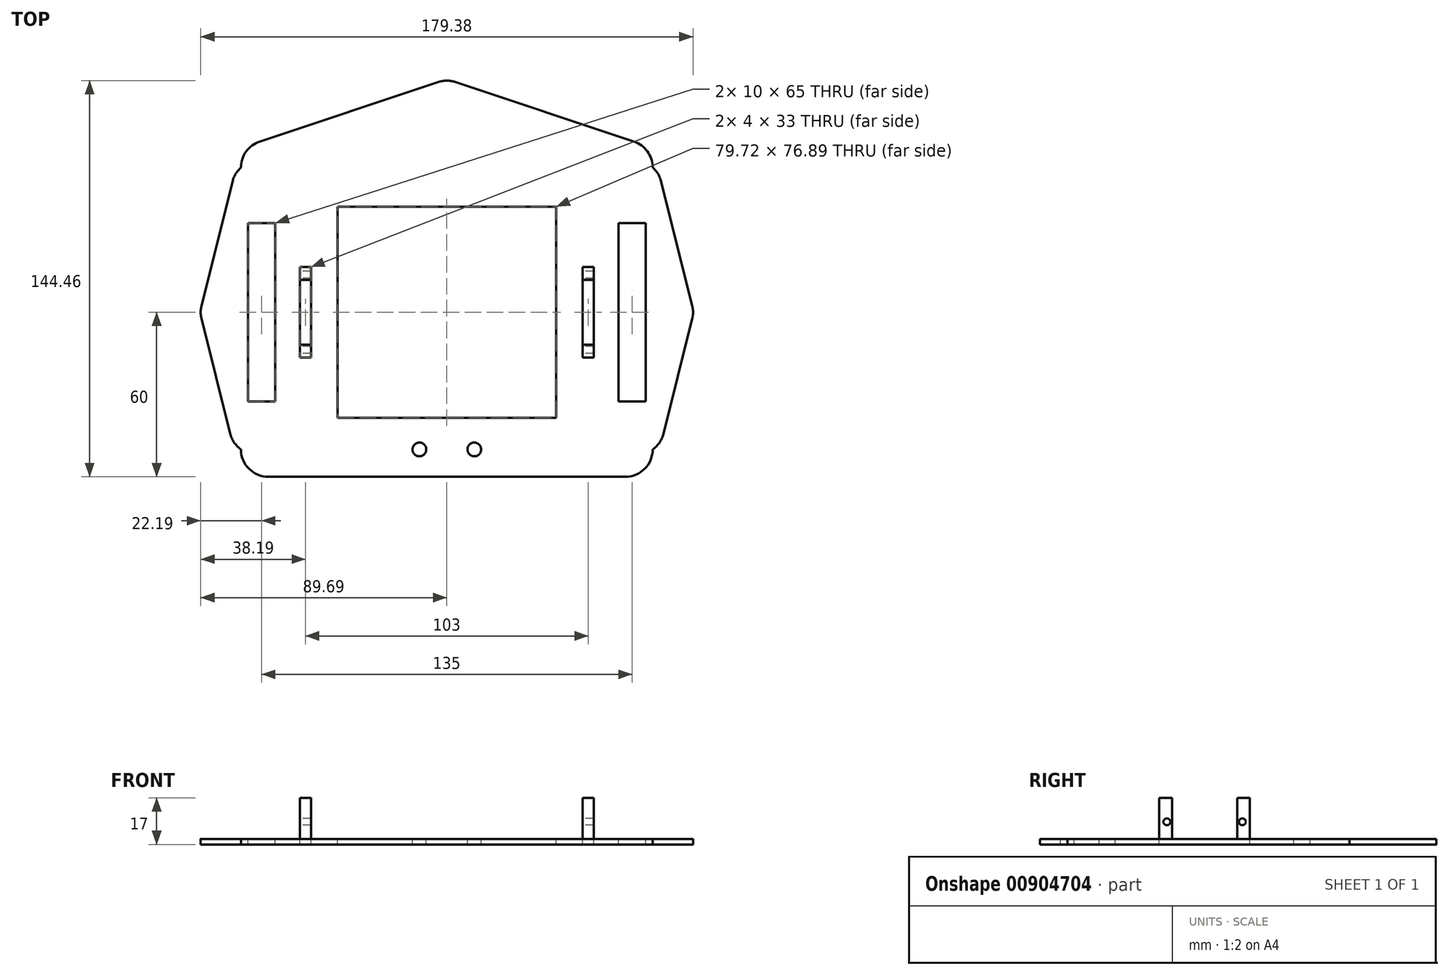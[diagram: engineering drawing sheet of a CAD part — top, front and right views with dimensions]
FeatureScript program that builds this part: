
annotation { "Feature Type Name" : "Feature", "Feature Type Description" : "" }
export const myFeature = defineFeature(function(context is Context, id is Id, definition is map)
    precondition{}
    {
        {
            var Q0;
            Q0=qCreatedBy(makeId("Top.planeOp"),FACE);
            var sketch = newSketch(context, id + "F0", { "sketchPlane" : qUnion([Q0])});
            skLineSegment(sketch, "E0.bottom", {"start": v(-75, 60) * mm, "end": v(75, 60) * mm});
            skLineSegment(sketch, "E0.top", {"start": v(-75, -60) * mm, "end": v(75, -60) * mm});
            skLineSegment(sketch, "E0.left", {"start": v(-75, 60) * mm, "end": v(-75, -60) * mm});
            skLineSegment(sketch, "E0.right", {"start": v(75, 60) * mm, "end": v(75, -60) * mm});
            skPoint(sketch, "E0.middle", {"position": v(0, 0) * mm});
            skLineSegment(sketch, "E1", {"start": v(-75, 0) * mm, "end": v(75, 0) * mm, "construction": true});
            skLineSegment(sketch, "E2.bottom", {"start": v(-62.5, 32.5) * mm, "end": v(-72.5, 32.5) * mm});
            skLineSegment(sketch, "E2.top", {"start": v(-62.5, -32.5) * mm, "end": v(-72.5, -32.5) * mm});
            skLineSegment(sketch, "E2.left", {"start": v(-62.5, 32.5) * mm, "end": v(-62.5, -32.5) * mm});
            skLineSegment(sketch, "E2.right", {"start": v(-72.5, 32.5) * mm, "end": v(-72.5, -32.5) * mm});
            skPoint(sketch, "E2.middle", {"position": v(-67.5, 0) * mm});
            skLineSegment(sketch, "E3.bottom", {"start": v(62.5, 32.5) * mm, "end": v(72.5, 32.5) * mm});
            skLineSegment(sketch, "E3.top", {"start": v(62.5, -32.5) * mm, "end": v(72.5, -32.5) * mm});
            skLineSegment(sketch, "E3.left", {"start": v(62.5, 32.5) * mm, "end": v(62.5, -32.5) * mm});
            skLineSegment(sketch, "E3.right", {"start": v(72.5, 32.5) * mm, "end": v(72.5, -32.5) * mm});
            skPoint(sketch, "E3.middle", {"position": v(67.5, 0) * mm});
            skLineSegment(sketch, "E4.bottom", {"start": v(-49.5, 16.5) * mm, "end": v(-53.5, 16.5) * mm});
            skLineSegment(sketch, "E4.top", {"start": v(-49.5, -16.5) * mm, "end": v(-53.5, -16.5) * mm});
            skLineSegment(sketch, "E4.left", {"start": v(-49.5, 16.5) * mm, "end": v(-49.5, -16.5) * mm});
            skLineSegment(sketch, "E4.right", {"start": v(-53.5, 16.5) * mm, "end": v(-53.5, -16.5) * mm});
            skPoint(sketch, "E4.middle", {"position": v(-51.5, 0) * mm});
            skLineSegment(sketch, "E5.bottom", {"start": v(49.5, 16.5) * mm, "end": v(53.5, 16.5) * mm});
            skLineSegment(sketch, "E5.top", {"start": v(49.5, -16.5) * mm, "end": v(53.5, -16.5) * mm});
            skLineSegment(sketch, "E5.left", {"start": v(49.5, 16.5) * mm, "end": v(49.5, -16.5) * mm});
            skLineSegment(sketch, "E5.right", {"start": v(53.5, 16.5) * mm, "end": v(53.5, -16.5) * mm});
            skPoint(sketch, "E5.middle", {"position": v(51.5, 0) * mm});
            skPoint(sketch, "E6", {"position": v(0, -60) * mm});
            skPoint(sketch, "E7", {"position": v(0, -55) * mm});
            skPoint(sketch, "E8", {"position": v(-10, -50) * mm});
            skPoint(sketch, "E9", {"position": v(10, -50) * mm});
            skLineSegment(sketch, "E10", {"start": v(0, 0) * mm, "end": v(0, -60) * mm});
            skCircle(sketch, "E11", {"center": v(-10, -50) * mm, "radius": 2.5 * mm});
            skCircle(sketch, "E12", {"center": v(10, -50) * mm, "radius": 2.5 * mm});
            skLineSegment(sketch, "E13.left", {"start": v(-49.5, 12) * mm, "end": v(-49.5, -12) * mm});
            skLineSegment(sketch, "E14.top", {"start": v(49.5, -12) * mm, "end": v(33.5, -12) * mm, "construction": true});
            skLineSegment(sketch, "E14.left", {"start": v(49.5, 12) * mm, "end": v(49.5, -12) * mm});
            skPoint(sketch, "E15", {"position": v(0, -42.33) * mm});
            skPoint(sketch, "E16", {"position": v(0, 60) * mm});
            skLineSegment(sketch, "E17", {"start": v(0, 60) * mm, "end": v(0, 85) * mm});
            skLineSegment(sketch, "E18", {"start": v(-75, 60) * mm, "end": v(0, 85) * mm});
            skLineSegment(sketch, "E19", {"start": v(75, 60) * mm, "end": v(0, 85) * mm});
            skPoint(sketch, "E20", {"position": v(-90, 0) * mm});
            skPoint(sketch, "E21", {"position": v(90, 0) * mm});
            skLineSegment(sketch, "E22", {"start": v(-75, -60) * mm, "end": v(-90, 0) * mm});
            skLineSegment(sketch, "E23", {"start": v(-75, 60) * mm, "end": v(-90, 0) * mm});
            skLineSegment(sketch, "E24", {"start": v(75, -60) * mm, "end": v(90, 0) * mm});
            skLineSegment(sketch, "E25", {"start": v(75, 60) * mm, "end": v(90, 0) * mm});
            skLineSegment(sketch, "E26.bottom", {"start": v(-39.86, 38.44) * mm, "end": v(39.86, 38.44) * mm});
            skLineSegment(sketch, "E26.top", {"start": v(-39.86, -38.44) * mm, "end": v(39.86, -38.44) * mm});
            skLineSegment(sketch, "E26.left", {"start": v(-39.86, 38.44) * mm, "end": v(-39.86, -38.44) * mm});
            skLineSegment(sketch, "E26.right", {"start": v(39.86, 38.44) * mm, "end": v(39.86, -38.44) * mm});
            skSolve(sketch);
        }
        {
            var Q0;
            {var subQ2=sQuery(id+"F0.wireOp",EDGE,"E17");Q0=makeQuery(id+"F0.imprint","IMPRINT",FACE,{"disambiguationData":[TD([[makeQuery(id+"F0.imprint","IMPRINT",EDGE,{"derivedFrom":subQ2}),1.0]])]});}
            var Q1;
            {var subQ2=sQuery(id+"F0.wireOp",EDGE,"E17");Q1=makeQuery(id+"F0.imprint","IMPRINT",FACE,{"disambiguationData":[TD([[makeQuery(id+"F0.imprint","IMPRINT",EDGE,{"derivedFrom":subQ2}),-1.0]])]});}
            var Q2;
            {var subQ11=sQuery(id+"F0.wireOp",EDGE,"E0.left");Q2=makeQuery(id+"F0.imprint","IMPRINT",FACE,{"disambiguationData":[TD([[makeQuery(id+"F0.imprint","IMPRINT",EDGE,{"derivedFrom":subQ11}),1.0]])]});}
            extrude(context, id + "F1", {"entities" : qUnion([Q0, Q1, Q2]), "oppositeDirection" : true, "depth" : 2 * mm, "offsetDistance" : 25 * mm});
        }
        {
            var Q0;
            {var subQ3=sQuery(id+"F0.wireOp",EDGE,"E4.bottom");Q0=makeQuery(id+"F0.imprint","IMPRINT",FACE,{"disambiguationData":[TD([[makeQuery(id+"F0.imprint","IMPRINT",EDGE,{"derivedFrom":subQ3}),1.0]])]});}
            var Q1;
            {var subQ3=sQuery(id+"F0.wireOp",EDGE,"E5.bottom");Q1=makeQuery(id+"F0.imprint","IMPRINT",FACE,{"disambiguationData":[TD([[makeQuery(id+"F0.imprint","IMPRINT",EDGE,{"derivedFrom":subQ3}),-1.0]])]});}
            extrude(context, id + "F2", {"entities" : qUnion([Q0, Q1]), "depth" : 15 * mm, "offsetDistance" : 25 * mm});
        }
        {
            var Q0;
            Q0=makeQuery(id+"F1.opExtrude","SWEPT_EDGE",EDGE,{"disambiguationData":[OSD([sQuery(id+"F0.wireOp",EDGE,"E0.top"),sQuery(id+"F0.wireOp",EDGE,"E0.left")])]});
            var Q1;
            Q1=makeQuery(id+"F1.opExtrude","SWEPT_EDGE",EDGE,{"disambiguationData":[OSD([sQuery(id+"F0.wireOp",EDGE,"E0.top"),sQuery(id+"F0.wireOp",EDGE,"E0.right")])]});
            var Q2;
            Q2=makeQuery(id+"F1.opExtrude","SWEPT_EDGE",EDGE,{"disambiguationData":[OSD([sQuery(id+"F0.wireOp",EDGE,"E0.bottom"),sQuery(id+"F0.wireOp",EDGE,"E0.right"),sQuery(id+"F0.wireOp",EDGE,"E19")])]});
            var Q3;
            Q3=makeQuery(id+"F1.opExtrude","SWEPT_EDGE",EDGE,{"disambiguationData":[OSD([sQuery(id+"F0.wireOp",EDGE,"E17"),sQuery(id+"F0.wireOp",EDGE,"E18"),sQuery(id+"F0.wireOp",EDGE,"E19")])]});
            var Q4;
            Q4=makeQuery(id+"F1.opExtrude","SWEPT_EDGE",EDGE,{"disambiguationData":[OSD([sQuery(id+"F0.wireOp",EDGE,"E0.bottom"),sQuery(id+"F0.wireOp",EDGE,"E0.left"),sQuery(id+"F0.wireOp",EDGE,"E18")])]});
            fillet(context, id + "F3", {"entities" : qUnion([Q0, Q1, Q2, Q3, Q4]), "radius" : 10 * mm, "tangentPropagation" : true, "allowEdgeOverflow" : false});
        }
        {
            var Q0;
            Q0=makeQuery(id+"F2.opExtrude","SWEPT_FACE",FACE,{"disambiguationData":[OSD([sQuery(id+"F0.wireOp",EDGE,"E4.right")])]});
            var sketch = newSketch(context, id + "F4", { "sketchPlane" : qUnion([Q0])});
            skLineSegment(sketch, "E27", {"start": v(0, 15) * mm, "end": v(-11.85, 15) * mm});
            skPoint(sketch, "E27.startSnap0", {"position": v(0, 0) * mm});
            skLineSegment(sketch, "E28", {"start": v(0, 15) * mm, "end": v(11.85, 15) * mm});
            skLineSegment(sketch, "E29", {"start": v(-11.85, 15) * mm, "end": v(-11.85, 0) * mm});
            skLineSegment(sketch, "E30", {"start": v(11.85, 15) * mm, "end": v(11.85, 0) * mm});
            skPoint(sketch, "E31", {"position": v(-13.75, 6.25) * mm});
            skPoint(sketch, "E32", {"position": v(0, 6.25) * mm});
            skPoint(sketch, "E33", {"position": v(13.75, 6.25) * mm});
            skCircle(sketch, "E34", {"center": v(-13.75, 6.25) * mm, "radius": 1.25 * mm});
            skCircle(sketch, "E35", {"center": v(13.75, 6.25) * mm, "radius": 1.25 * mm});
            skSolve(sketch);
        }
        {
            var Q0;
            Q0 = qSketchRegion(id + "F4", true);
            var Q1;
            Q1=makeQuery(id+"F4.imprint","IMPRINT",FACE,{"disambiguationData":[TD([[makeQuery(id+"F4.imprint","IMPRINT",EDGE,{"derivedFrom":sQuery(id+"F4.wireOp",EDGE,"E27")}),-1.0]])]});
            extrude(context, id + "F5", {"entities" : qUnion([Q0, Q1]), "operationType" : NewBodyOperationType.REMOVE, "oppositeDirection" : true, "depth" : 4.4 * mm, "offsetDistance" : 25 * mm});
        }
        {
            var Q0;
            {var subQ3=sQuery(id+"F0.wireOp",EDGE,"E5.bottom");Q0=makeQuery(id+"F0.imprint","IMPRINT",FACE,{"disambiguationData":[TD([[makeQuery(id+"F0.imprint","IMPRINT",EDGE,{"derivedFrom":subQ3}),-1.0]])]});}
            var Q1;
            {var subQ3=sQuery(id+"F0.wireOp",EDGE,"E4.bottom");Q1=makeQuery(id+"F0.imprint","IMPRINT",FACE,{"disambiguationData":[TD([[makeQuery(id+"F0.imprint","IMPRINT",EDGE,{"derivedFrom":subQ3}),1.0]])]});}
            extrude(context, id + "F6", {"entities" : qUnion([Q0, Q1]), "oppositeDirection" : true, "depth" : 2 * mm, "offsetDistance" : 25 * mm});
        }
        {
            var Q0;
            Q0=makeQuery(id+"F2.opExtrude","SWEPT_FACE",FACE,{"disambiguationData":[OSD([sQuery(id+"F0.wireOp",EDGE,"E5.left"),sQuery(id+"F0.wireOp",EDGE,"E14.left")])]});
            var sketch = newSketch(context, id + "F7", { "sketchPlane" : qUnion([Q0])});
            skPoint(sketch, "E36", {"position": v(0, 6.25) * mm});
            skPoint(sketch, "E37", {"position": v(-11.85, 6.25) * mm});
            skPoint(sketch, "E38", {"position": v(-13.75, 6.25) * mm});
            skPoint(sketch, "E39", {"position": v(11.85, 6.25) * mm});
            skPoint(sketch, "E40", {"position": v(13.75, 6.25) * mm});
            skCircle(sketch, "E41", {"center": v(-13.75, 6.25) * mm, "radius": 1.25 * mm});
            skCircle(sketch, "E42", {"center": v(13.75, 6.25) * mm, "radius": 1.25 * mm});
            skLineSegment(sketch, "E43", {"start": v(-11.85, 0) * mm, "end": v(-11.85, 15) * mm});
            skLineSegment(sketch, "E44", {"start": v(11.85, 0) * mm, "end": v(11.85, 15) * mm});
            skSolve(sketch);
        }
        {
            var Q0;
            Q0=makeQuery(id+"F7.imprint","IMPRINT",FACE,{"disambiguationData":[TD([[makeQuery(id+"F7.imprint","IMPRINT",EDGE,{"derivedFrom":sQuery(id+"F7.wireOp",EDGE,"E41")}),1.0]])]});
            var Q1;
            Q1=makeQuery(id+"F7.imprint","IMPRINT",FACE,{"disambiguationData":[TD([[makeQuery(id+"F7.imprint","IMPRINT",EDGE,{"derivedFrom":sQuery(id+"F7.wireOp",EDGE,"E42")}),1.0]])]});
            extrude(context, id + "F8", {"entities" : qUnion([Q0, Q1]), "operationType" : NewBodyOperationType.REMOVE, "oppositeDirection" : true, "depth" : 4.7 * mm, "offsetDistance" : 25 * mm});
        }
        {
            var Q0;
            {var subQ0=sQuery(id+"F7.wireOp",EDGE,"E43");Q0=makeQuery(id+"F7.imprint","IMPRINT",FACE,{"disambiguationData":[TD([[makeQuery(id+"F7.imprint","IMPRINT",EDGE,{"derivedFrom":subQ0}),-1.0]])]});}
            extrude(context, id + "F9", {"entities" : qUnion([Q0]), "operationType" : NewBodyOperationType.REMOVE, "oppositeDirection" : true, "depth" : 4.3 * mm, "offsetDistance" : 25 * mm});
        }
        {
            var Q0;
            Q0=makeQuery(id+"F0.imprint","IMPRINT",FACE,{"disambiguationData":[TD([[makeQuery(id+"F0.imprint","IMPRINT",EDGE,{"derivedFrom":sQuery(id+"F0.wireOp",EDGE,"E0.left")}),-1.0]])]});
            var Q1;
            Q1=makeQuery(id+"F0.imprint","IMPRINT",FACE,{"disambiguationData":[TD([[makeQuery(id+"F0.imprint","IMPRINT",EDGE,{"derivedFrom":sQuery(id+"F0.wireOp",EDGE,"E0.right")}),1.0]])]});
            extrude(context, id + "F10", {"entities" : qUnion([Q0, Q1]), "operationType" : NewBodyOperationType.ADD, "oppositeDirection" : true, "depth" : 2 * mm, "offsetDistance" : 25 * mm});
        }
        {
            var Q0;
            Q0=makeQuery(id+"F10.opExtrude","SWEPT_EDGE",EDGE,{"disambiguationData":[OSD([sQuery(id+"F0.wireOp",EDGE,"E0.top"),sQuery(id+"F0.wireOp",EDGE,"E0.left"),sQuery(id+"F0.wireOp",EDGE,"E22")])]});
            var Q1;
            Q1=makeQuery(id+"F10.opExtrude","SWEPT_EDGE",EDGE,{"disambiguationData":[OSD([sQuery(id+"F0.wireOp",EDGE,"E0.top"),sQuery(id+"F0.wireOp",EDGE,"E0.right"),sQuery(id+"F0.wireOp",EDGE,"E24")])]});
            var Q2;
            Q2=makeQuery(id+"F10.opExtrude","SWEPT_EDGE",EDGE,{"disambiguationData":[OSD([sQuery(id+"F0.wireOp",EDGE,"E0.bottom"),sQuery(id+"F0.wireOp",EDGE,"E0.right"),sQuery(id+"F0.wireOp",EDGE,"E19"),sQuery(id+"F0.wireOp",EDGE,"E25")])]});
            var Q3;
            Q3=makeQuery(id+"F10.opExtrude","SWEPT_EDGE",EDGE,{"disambiguationData":[OSD([sQuery(id+"F0.wireOp",EDGE,"E0.bottom"),sQuery(id+"F0.wireOp",EDGE,"E0.left"),sQuery(id+"F0.wireOp",EDGE,"E18"),sQuery(id+"F0.wireOp",EDGE,"E23")])]});
            var Q4;
            Q4=makeQuery(id+"F10.opExtrude","SWEPT_EDGE",EDGE,{"disambiguationData":[OSD([sQuery(id+"F0.wireOp",EDGE,"E24"),sQuery(id+"F0.wireOp",EDGE,"E25")])]});
            var Q5;
            Q5=makeQuery(id+"F10.opExtrude","SWEPT_EDGE",EDGE,{"disambiguationData":[OSD([sQuery(id+"F0.wireOp",EDGE,"E22"),sQuery(id+"F0.wireOp",EDGE,"E23")])]});
            fillet(context, id + "F11", {"entities" : qUnion([Q0, Q1, Q2, Q3, Q4, Q5]), "radius" : 10 * mm, "tangentPropagation" : true, "allowEdgeOverflow" : false});
        }
    });
